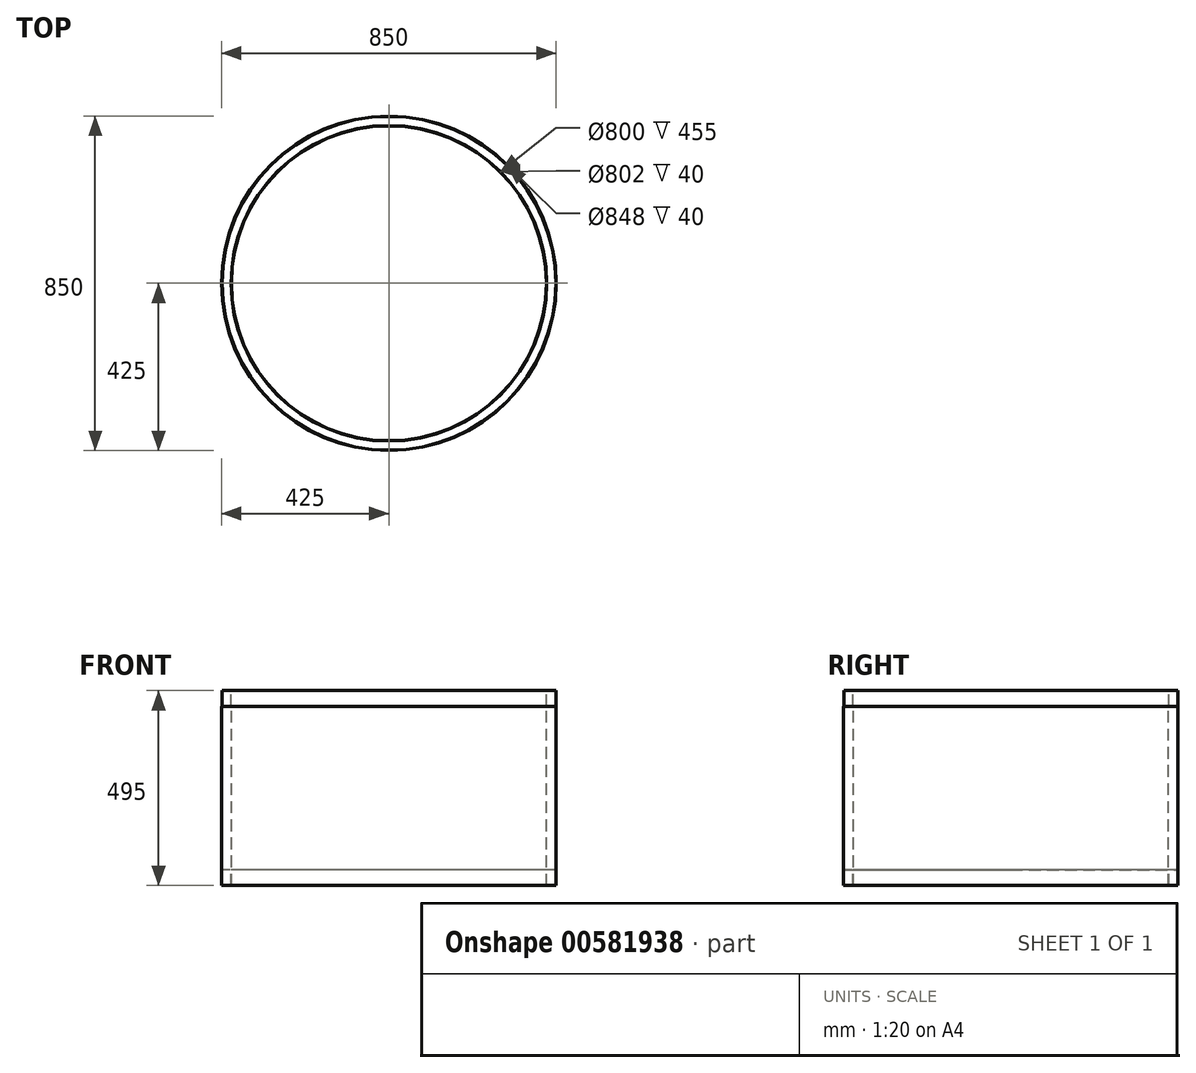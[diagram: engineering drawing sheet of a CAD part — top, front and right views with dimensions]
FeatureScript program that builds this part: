
annotation { "Feature Type Name" : "Feature", "Feature Type Description" : "" }
export const myFeature = defineFeature(function(context is Context, id is Id, definition is map)
    precondition{}
    {
        {
            var Q0;
            Q0=qCreatedBy(makeId("Front.planeOp"),FACE);
            var sketch = newSketch(context, id + "F0", { "sketchPlane" : qUnion([Q0])});
            skLineSegment(sketch, "E0", {"start": v(0, 345.75) * mm, "end": v(0, -558.03) * mm, "construction": true});
            skLineSegment(sketch, "E1", {"start": v(-400, -518.84) * mm, "end": v(-400, -63.84) * mm});
            skLineSegment(sketch, "E2", {"start": v(-400, -63.84) * mm, "end": v(-401, -63.84) * mm});
            skLineSegment(sketch, "E3", {"start": v(-401, -63.84) * mm, "end": v(-401, -23.84) * mm});
            skLineSegment(sketch, "E4", {"start": v(-401, -23.84) * mm, "end": v(-424, -23.84) * mm});
            skLineSegment(sketch, "E5", {"start": v(-424, -23.84) * mm, "end": v(-424, -63.84) * mm});
            skLineSegment(sketch, "E6", {"start": v(-424, -63.84) * mm, "end": v(-425, -63.84) * mm});
            skLineSegment(sketch, "E7", {"start": v(-425, -63.84) * mm, "end": v(-425, -518.84) * mm});
            skLineSegment(sketch, "E8", {"start": v(-425, -518.84) * mm, "end": v(-424, -518.84) * mm});
            skLineSegment(sketch, "E9", {"start": v(-424, -518.84) * mm, "end": v(-424, -478.84) * mm});
            skLineSegment(sketch, "E10", {"start": v(-424, -478.84) * mm, "end": v(-401, -478.84) * mm});
            skLineSegment(sketch, "E11", {"start": v(-401, -478.84) * mm, "end": v(-401, -518.84) * mm});
            skLineSegment(sketch, "E12", {"start": v(-401, -518.84) * mm, "end": v(-400, -518.84) * mm});
            skSolve(sketch);
        }
        {
            var Q0;
            Q0=qSketchRegion(id+"F0",true);
            var Q1;
            Q1=sQuery(id+"F0.wireOp",EDGE,"E0");
            revolve(context, id + "F1", {"entities" : qUnion([Q0]), "axis" : qUnion([Q1]), "revolveType" : RevolveType.FULL});
        }
    });
